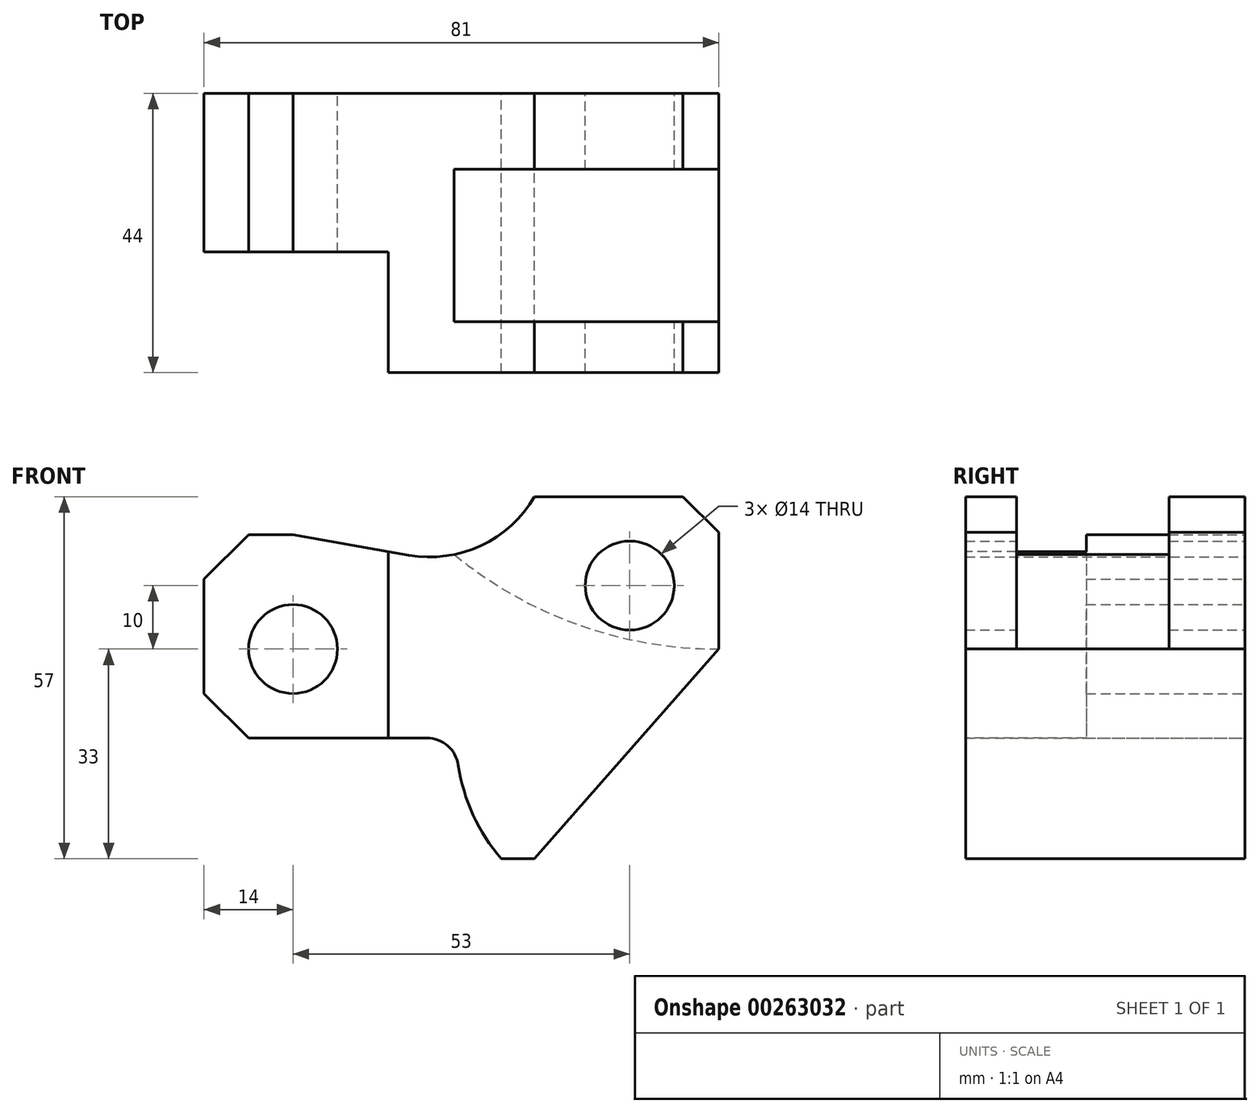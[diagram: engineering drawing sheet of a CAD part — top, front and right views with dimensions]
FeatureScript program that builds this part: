
annotation { "Feature Type Name" : "Feature", "Feature Type Description" : "" }
export const myFeature = defineFeature(function(context is Context, id is Id, definition is map)
    precondition{}
    {
        {
            var Q0;
            Q0=qCreatedBy(makeId("Front.planeOp"),FACE);
            var sketch = newSketch(context, id + "F0", { "sketchPlane" : qUnion([Q0])});
            skCircle(sketch, "E0", {"center": v(0, 0) * mm, "radius": 7 * mm});
            skLineSegment(sketch, "E1", {"start": v(-14, 11) * mm, "end": v(-14, -7) * mm});
            skLineSegment(sketch, "E2", {"start": v(-14, -7) * mm, "end": v(-7, -14) * mm});
            skLineSegment(sketch, "E3", {"start": v(-7, -14) * mm, "end": v(21.07, -14) * mm});
            skLineSegment(sketch, "E4", {"start": v(32.79, -33) * mm, "end": v(38, -33) * mm});
            skLineSegment(sketch, "E5", {"start": v(0, 18) * mm, "end": v(-7, 18) * mm});
            skLineSegment(sketch, "E6", {"start": v(-7, 18) * mm, "end": v(-14, 11) * mm});
            skLineSegment(sketch, "E7", {"start": v(38, 24) * mm, "end": v(61.35, 24) * mm});
            skLineSegment(sketch, "E8", {"start": v(61.35, 24) * mm, "end": v(67, 18.35) * mm});
            skLineSegment(sketch, "E9", {"start": v(0, 18) * mm, "end": v(18.24, 14.78) * mm});
            skArc(sketch, "E10", {"start": v(18.24, 14.78) * mm, "mid": v(29.57, 16.28) * mm, "end": v(38, 24) * mm});
            skLineSegment(sketch, "E11", {"start": v(67, 18.35) * mm, "end": v(67, 0) * mm});
            skLineSegment(sketch, "E12", {"start": v(67, 0) * mm, "end": v(38, -33) * mm});
            skPoint(sketch, "E13.startSnap0", {"position": v(-3.5, 18) * mm});
            skArc(sketch, "E14", {"start": v(26.01, -18.26) * mm, "mid": v(24.33, -15.21) * mm, "end": v(21.07, -14) * mm});
            skArc(sketch, "E15", {"start": v(26.01, -18.26) * mm, "mid": v(28.35, -26.12) * mm, "end": v(32.79, -33) * mm});
            skCircle(sketch, "E16", {"center": v(53, 10) * mm, "radius": 7 * mm});
            skSolve(sketch);
        }
        {
            var Q0;
            Q0=makeQuery(id+"F0.imprint","IMPRINT",FACE,{"disambiguationData":[TD([[makeQuery(id+"F0.imprint","IMPRINT",EDGE,{"derivedFrom":sQuery(id+"F0.wireOp",EDGE,"E0")}),-1.0]])]});
            extrude(context, id + "F1", {"entities" : qUnion([Q0]), "endBound" : BoundingType.SYMMETRIC, "depth" : 44 * mm});
        }
        {
            var Q0;
            Q0=qCreatedBy(makeId("Top.planeOp"),FACE);
            var sketch = newSketch(context, id + "F2", { "sketchPlane" : qUnion([Q0])});
            skLineSegment(sketch, "E17", {"start": v(90.38, 10) * mm, "end": v(25.36, 10) * mm});
            skLineSegment(sketch, "E18", {"start": v(25.36, 10) * mm, "end": v(25.36, -14) * mm});
            skLineSegment(sketch, "E19", {"start": v(25.36, -14) * mm, "end": v(90.38, -14) * mm});
            skLineSegment(sketch, "E20", {"start": v(90.38, -14) * mm, "end": v(90.38, 10) * mm});
            skLineSegment(sketch, "E21", {"start": v(-25.42, -3) * mm, "end": v(-25.42, -24.6) * mm});
            skLineSegment(sketch, "E22", {"start": v(-25.42, -24.6) * mm, "end": v(15, -24.6) * mm});
            skLineSegment(sketch, "E23", {"start": v(15, -24.6) * mm, "end": v(15, -3) * mm});
            skLineSegment(sketch, "E24", {"start": v(15, -3) * mm, "end": v(-25.42, -3) * mm});
            skLineSegment(sketch, "E25", {"start": v(37.76, 0) * mm, "end": v(86.16, 0) * mm});
            skLineSegment(sketch, "E26", {"start": v(86.16, 0) * mm, "end": v(86.16, -24.64) * mm});
            skSolve(sketch);
        }
        {
            var Q0;
            Q0=makeQuery(id+"F2.imprint","IMPRINT",FACE,{"disambiguationData":[TD([[makeQuery(id+"F2.imprint","IMPRINT",EDGE,{"derivedFrom":sQuery(id+"F2.wireOp",EDGE,"E17")}),1.0]])]});
            extrude(context, id + "F3", {"entities" : qUnion([Q0]), "operationType" : NewBodyOperationType.REMOVE, "depth" : 69.1 * mm});
        }
        {
            var Q0;
            Q0=makeQuery(id+"F3.boolean.opBoolean","COPY",EDGE,{"derivedFrom":makeQuery(id+"F3.opExtrude","CAP_EDGE",EDGE,{"disambiguationData":[OSD([sQuery(id+"F2.wireOp",EDGE,"E18")])],"isStart":true})});
            fillet(context, id + "F4", {"entities" : qUnion([Q0]), "radius" : 65.7 * mm, "tangentPropagation" : true, "allowEdgeOverflow" : false});
        }
        {
            var Q0;
            Q0=makeQuery(id+"F2.imprint","IMPRINT",FACE,{"disambiguationData":[TD([[makeQuery(id+"F2.imprint","IMPRINT",EDGE,{"derivedFrom":sQuery(id+"F2.wireOp",EDGE,"E21")}),1.0]])]});
            extrude(context, id + "F5", {"entities" : qUnion([Q0]), "operationType" : NewBodyOperationType.REMOVE, "endBound" : BoundingType.SYMMETRIC, "depth" : 144.4 * mm});
        }
    });
